# Revit family: LSVB48
name_source: partatom
category: Lighting Fixtures
units: mm (PartAtom-declared; Revit-internal decimal feet)

## family parameters
Always vertical = Yes
Cut with Voids When Loaded = No
Host = Ceiling
Light Source = Yes
OmniClass Number = 23.80.70.11
OmniClass Title = Luminaries for Internal Lighting
Part Type = Normal
Room Calculation Point = No
Round Connector Dimension = Use Diameter
Shared = No

## types (4) — shared parameters
Assembly Code = D5020200
Color Filter = 16777215
Description = LED Sealed Vapour B
Dimming Lamp Color Temperature Shift = <None>
Emit from Line Length = 3' - 11 1/4"
Housing Finish = Metal - Viscor - White
Lamp = LED
Length = 3' - 11 1/4"
Lens Finsih = Polycarbonate - Viscor - Frosted Round
Manufacturer = VISIONEERING by VISCOR
Model = LSVB48
Tilt Angle = 90.00°
URL = https://www.viscor.com
Voltage = 120 V
Width = 0' - 3 7/8"

## per-type parameters (varying)
| type | Apparent Load | Lamp Wattage | Photometric Web File |
| LSVB48-LED840K030LUNV | 22 VA | 22 VA | LSVB48-LED840K030LUNV.IES |
| LSVB48-LED840K055LUNV | 41 VA | 41 VA | LSVB48-LED840K055LUNV.IES |
| LSVB48-LED840K040LUNV | 29 VA | 29 VA | LSVB48-LED840K040LUNV.IES |
| LSVB48-LED840K070LUNV | 53 VA | 53 VA | LSVB48-LED840K070LUNV.IES |

## geometry (parser evidence)
native form markers: Sweep x3
no freeform markers — native parametric forms only
